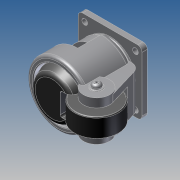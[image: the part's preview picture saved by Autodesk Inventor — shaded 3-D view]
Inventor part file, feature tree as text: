
AUTODESK INVENTOR PART (.ipt)
format: ipt  version: 2016 (Build 200138000, 138)  size: 537,600 bytes
history: native  units: mm
features: sketch x17, extrude x13, other x7, revolve x3, hole x1
ambient origin geometry x8: Origin, YZ Plane, XZ Plane, XY Plane, X Axis, Y Axis, Z Axis, Center Point
bodies: Solid1 (feature_tree)
feature tree (41):
  sketch  "Sketch_2"  dims[d3=6.0mm d4=0.0mm d5=46.0mm d6=0.0mm]
  sketch  "Sketch_1"  dims[d0=42.0mm d1=0.0mm d2=360.0deg]
  extrude  "Extrusion1"  TaperAngle=360.0deg  [1 undecoded]
  revolve  "Revolution1"  [1 undecoded]
  extrude  "Extrusion2"  Depth=45.0mm TaperAngle=0.0deg
  sketch  "Sketch_5"  dims[d14=6.0mm d15=0.0mm d16=36.0mm d17=0.0mm]
  extrude  "Extrusion3"  Depth=6.0mm TaperAngle=0.0deg
  extrude  "Extrusion4"  Depth=36.0mm TaperAngle=0.0deg
  extrude  "Extrusion5"  Depth=7.0mm TaperAngle=0.0deg
  sketch  "Sketch_6"  dims[d18=48.0mm d19=0.0mm d20=7.0mm d21=0.0mm]
  revolve  "Revolution2"  [1 undecoded]
  extrude  "Extrusion6"  Depth=2.0mm TaperAngle=0.0deg
  extrude  "Extrusion7"  [1 undecoded]
  extrude  "Extrusion8"  [1 undecoded]
  extrude  "Extrusion9"  [1 undecoded]
  extrude  "Extrusion10"  [1 undecoded]
  extrude  "Extrusion11"  [1 undecoded]
  extrude  "Extrusion12"  [1 undecoded]
  hole  "Drilling 1"  [1 undecoded]
  extrude  "Extrusion13"  [1 undecoded]
  revolve  "Revolution3"  [1 undecoded]
  other  "start_XY"
  other  "start_YZ"
  other  "start_ZX"
  other  "start_X"
  other  "start_Y"
  other  "start_Z"
  other  "start_Center"
  sketch  "Sketch_3"  dims[d7=84.0mm d8=0.0mm d9=45.0mm d10=0.0mm]
  sketch  "Sketch_4"  dims[d11=360.0deg d12=6.0mm d13=0.0mm]
  sketch  "Sketch_7"  dims[d22=8.0mm d23=0.0mm d24=28.0mm d25=0.0mm]
  sketch  "Sketch_8"  dims[d26=14.5mm d27=6.0mm d28=4.0mm d29=2.0mm d30=90.0deg d31=19.0mm d32=0.0mm d33=2.0mm d34=0.0mm]
  sketch  "Sketch_9"  dims[d35=360.0deg]
  sketch  "Sketch_10"
  sketch  "Sketch_11"
  sketch  "Sketch_12"
  sketch  "Sketch_13"
  sketch  "Sketch_14"
  sketch  "Sketch_15"
  sketch  "Sketch16"
  sketch  "Sketch_17"
note: 12 required parameter values undecoded (feature->parameter linkage not recoverable at this tier; creation-order binding heuristic only, values carry confidence <= 0.55)